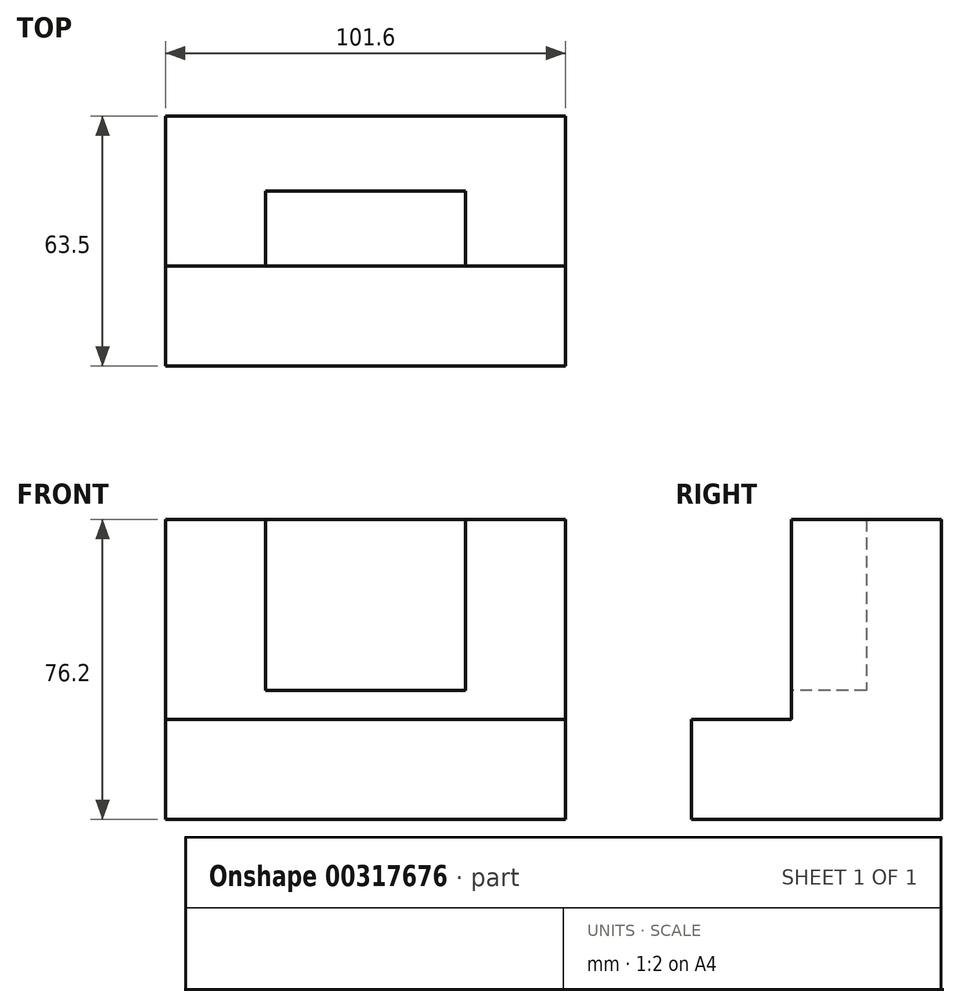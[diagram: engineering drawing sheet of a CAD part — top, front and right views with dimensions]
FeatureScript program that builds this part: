
annotation { "Feature Type Name" : "Feature", "Feature Type Description" : "" }
export const myFeature = defineFeature(function(context is Context, id is Id, definition is map)
    precondition{}
    {
        {
            var Q0;
            Q0=qCreatedBy(makeId("Right.planeOp"),FACE);
            var sketch = newSketch(context, id + "F0", { "sketchPlane" : qUnion([Q0])});
            skLineSegment(sketch, "E0", {"start": v(-31.75, -22.24) * mm, "end": v(31.75, -22.24) * mm});
            skLineSegment(sketch, "E1", {"start": v(-31.75, -22.24) * mm, "end": v(-31.75, 3.16) * mm});
            skLineSegment(sketch, "E2", {"start": v(-31.75, 3.16) * mm, "end": v(-6.35, 3.16) * mm});
            skLineSegment(sketch, "E3", {"start": v(-6.35, 3.16) * mm, "end": v(-6.35, 53.96) * mm});
            skLineSegment(sketch, "E4", {"start": v(-6.35, 53.96) * mm, "end": v(31.75, 53.96) * mm});
            skLineSegment(sketch, "E5", {"start": v(31.75, 53.96) * mm, "end": v(31.75, -22.24) * mm});
            skSolve(sketch);
        }
        {
            var Q0;
            Q0 = qSketchRegion(id + "F0", true);
            extrude(context, id + "F1", {"entities" : qUnion([Q0]), "oppositeDirection" : true, "depth" : 101.6 * mm});
        }
        {
            var Q0;
            Q0=makeQuery(id+"F1.opExtrude","SWEPT_FACE",FACE,{"disambiguationData":[OSD([sQuery(id+"F0.wireOp",EDGE,"E3")])]});
            var sketch = newSketch(context, id + "F2", { "sketchPlane" : qUnion([Q0])});
            skLineSegment(sketch, "E6.bottom", {"start": v(-76.2, 53.96) * mm, "end": v(-25.4, 53.96) * mm});
            skLineSegment(sketch, "E6.top", {"start": v(-76.2, 10.6) * mm, "end": v(-25.4, 10.6) * mm});
            skLineSegment(sketch, "E6.left", {"start": v(-76.2, 53.96) * mm, "end": v(-76.2, 10.6) * mm});
            skLineSegment(sketch, "E6.right", {"start": v(-25.4, 53.96) * mm, "end": v(-25.4, 10.6) * mm});
            skSolve(sketch);
        }
        {
            var Q0;
            Q0=makeQuery(id+"F2.imprint","IMPRINT",FACE,{"disambiguationData":[TD([[makeQuery(id+"F2.imprint","IMPRINT",EDGE,{"derivedFrom":sQuery(id+"F2.wireOp",EDGE,"E6.bottom")}),-1.0]])]});
            extrude(context, id + "F3", {"entities" : qUnion([Q0]), "operationType" : NewBodyOperationType.REMOVE, "oppositeDirection" : true, "depth" : 19.05 * mm});
        }
    });
